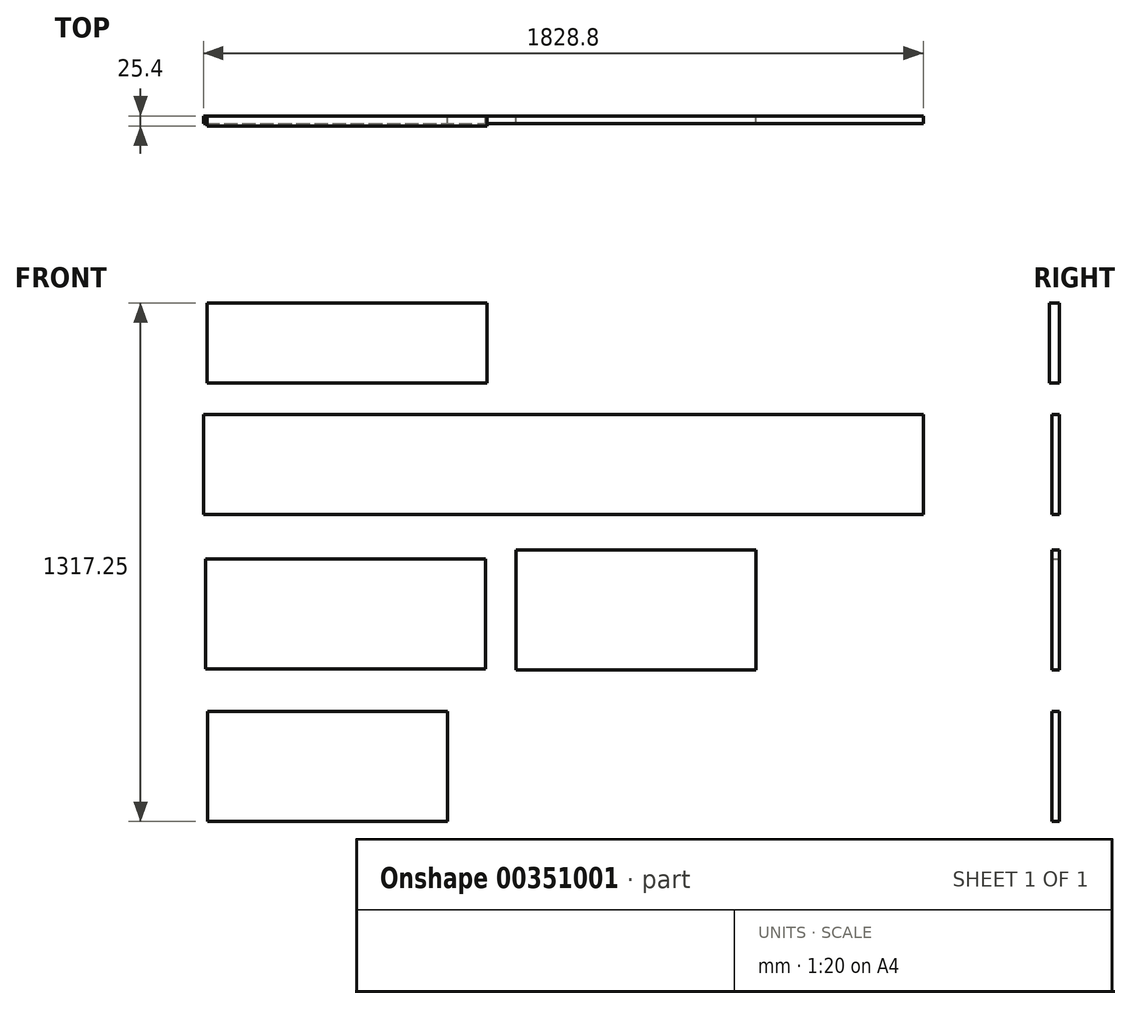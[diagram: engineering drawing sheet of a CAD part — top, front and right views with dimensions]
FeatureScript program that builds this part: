
annotation { "Feature Type Name" : "Feature", "Feature Type Description" : "" }
export const myFeature = defineFeature(function(context is Context, id is Id, definition is map)
    precondition{}
    {
        {
            var Q0;
            Q0=qCreatedBy(makeId("Front.planeOp"),FACE);
            var sketch = newSketch(context, id + "F0", { "sketchPlane" : qUnion([Q0])});
            skLineSegment(sketch, "E0.bottom", {"start": v(-582.17, 254) * mm, "end": v(1246.63, 254) * mm});
            skLineSegment(sketch, "E0.top", {"start": v(-582.17, 0) * mm, "end": v(1246.63, 0) * mm});
            skLineSegment(sketch, "E0.left", {"start": v(-582.17, 254) * mm, "end": v(-582.17, 0) * mm});
            skLineSegment(sketch, "E0.right", {"start": v(1246.63, 254) * mm, "end": v(1246.63, 0) * mm});
            skSolve(sketch);
        }
        {
            var Q0;
            Q0 = qSketchRegion(id + "F0", true);
            extrude(context, id + "F1", {"entities" : qUnion([Q0]), "depth" : 19.05 * mm});
        }
        {
            var Q0;
            Q0=qCreatedBy(makeId("Front.planeOp"),FACE);
            var sketch = newSketch(context, id + "F2", { "sketchPlane" : qUnion([Q0])});
            skLineSegment(sketch, "E1.bottom", {"start": v(-576.27, -112.92) * mm, "end": v(134.93, -112.92) * mm});
            skLineSegment(sketch, "E1.top", {"start": v(-576.27, -392.32) * mm, "end": v(134.93, -392.32) * mm});
            skLineSegment(sketch, "E1.left", {"start": v(-576.27, -112.92) * mm, "end": v(-576.27, -392.32) * mm});
            skLineSegment(sketch, "E1.right", {"start": v(134.93, -112.92) * mm, "end": v(134.93, -392.32) * mm});
            skSolve(sketch);
        }
        {
            var Q0;
            Q0=makeQuery(id+"F2.imprint","IMPRINT",FACE,{"disambiguationData":[TD([[makeQuery(id+"F2.imprint","IMPRINT",EDGE,{"derivedFrom":sQuery(id+"F2.wireOp",EDGE,"E1.bottom")}),-1.0]])]});
            extrude(context, id + "F3", {"entities" : qUnion([Q0]), "depth" : 19.05 * mm});
        }
        {
            var Q0;
            Q0=qCreatedBy(makeId("Front.planeOp"),FACE);
            var sketch = newSketch(context, id + "F4", { "sketchPlane" : qUnion([Q0])});
            skLineSegment(sketch, "E2.bottom", {"start": v(212.38, -90.06) * mm, "end": v(821.98, -90.06) * mm});
            skLineSegment(sketch, "E2.top", {"start": v(212.38, -394.86) * mm, "end": v(821.98, -394.86) * mm});
            skLineSegment(sketch, "E2.left", {"start": v(212.38, -90.06) * mm, "end": v(212.38, -394.86) * mm});
            skLineSegment(sketch, "E2.right", {"start": v(821.98, -90.06) * mm, "end": v(821.98, -394.86) * mm});
            skSolve(sketch);
        }
        {
            var Q0;
            Q0=makeQuery(id+"F4.imprint","IMPRINT",FACE,{"disambiguationData":[TD([[makeQuery(id+"F4.imprint","IMPRINT",EDGE,{"derivedFrom":sQuery(id+"F4.wireOp",EDGE,"E2.bottom")}),-1.0]])]});
            extrude(context, id + "F5", {"entities" : qUnion([Q0]), "depth" : 19.05 * mm});
        }
        {
            var Q0;
            Q0=qCreatedBy(makeId("Front.planeOp"),FACE);
            var sketch = newSketch(context, id + "F6", { "sketchPlane" : qUnion([Q0])});
            skLineSegment(sketch, "E3.bottom", {"start": v(-571.54, -500.52) * mm, "end": v(38.06, -500.52) * mm});
            skLineSegment(sketch, "E3.top", {"start": v(-571.54, -779.92) * mm, "end": v(38.06, -779.92) * mm});
            skLineSegment(sketch, "E3.left", {"start": v(-571.54, -500.52) * mm, "end": v(-571.54, -779.92) * mm});
            skLineSegment(sketch, "E3.right", {"start": v(38.06, -500.52) * mm, "end": v(38.06, -779.92) * mm});
            skSolve(sketch);
        }
        {
            var Q0;
            Q0 = qSketchRegion(id + "F6", true);
            extrude(context, id + "F7", {"entities" : qUnion([Q0]), "depth" : 19.05 * mm});
        }
        {
            var Q0;
            Q0=qCreatedBy(makeId("Front.planeOp"),FACE);
            var sketch = newSketch(context, id + "F8", { "sketchPlane" : qUnion([Q0])});
            skLineSegment(sketch, "E4.bottom", {"start": v(-573.27, 537.33) * mm, "end": v(137.93, 537.33) * mm});
            skLineSegment(sketch, "E4.top", {"start": v(-573.27, 334.13) * mm, "end": v(137.93, 334.13) * mm});
            skLineSegment(sketch, "E4.left", {"start": v(-573.27, 537.33) * mm, "end": v(-573.27, 334.13) * mm});
            skLineSegment(sketch, "E4.right", {"start": v(137.93, 537.33) * mm, "end": v(137.93, 334.13) * mm});
            skSolve(sketch);
        }
        {
            var Q0;
            Q0 = qSketchRegion(id + "F8", true);
            extrude(context, id + "F9", {"entities" : qUnion([Q0]), "depth" : 25.4 * mm});
        }
    });
